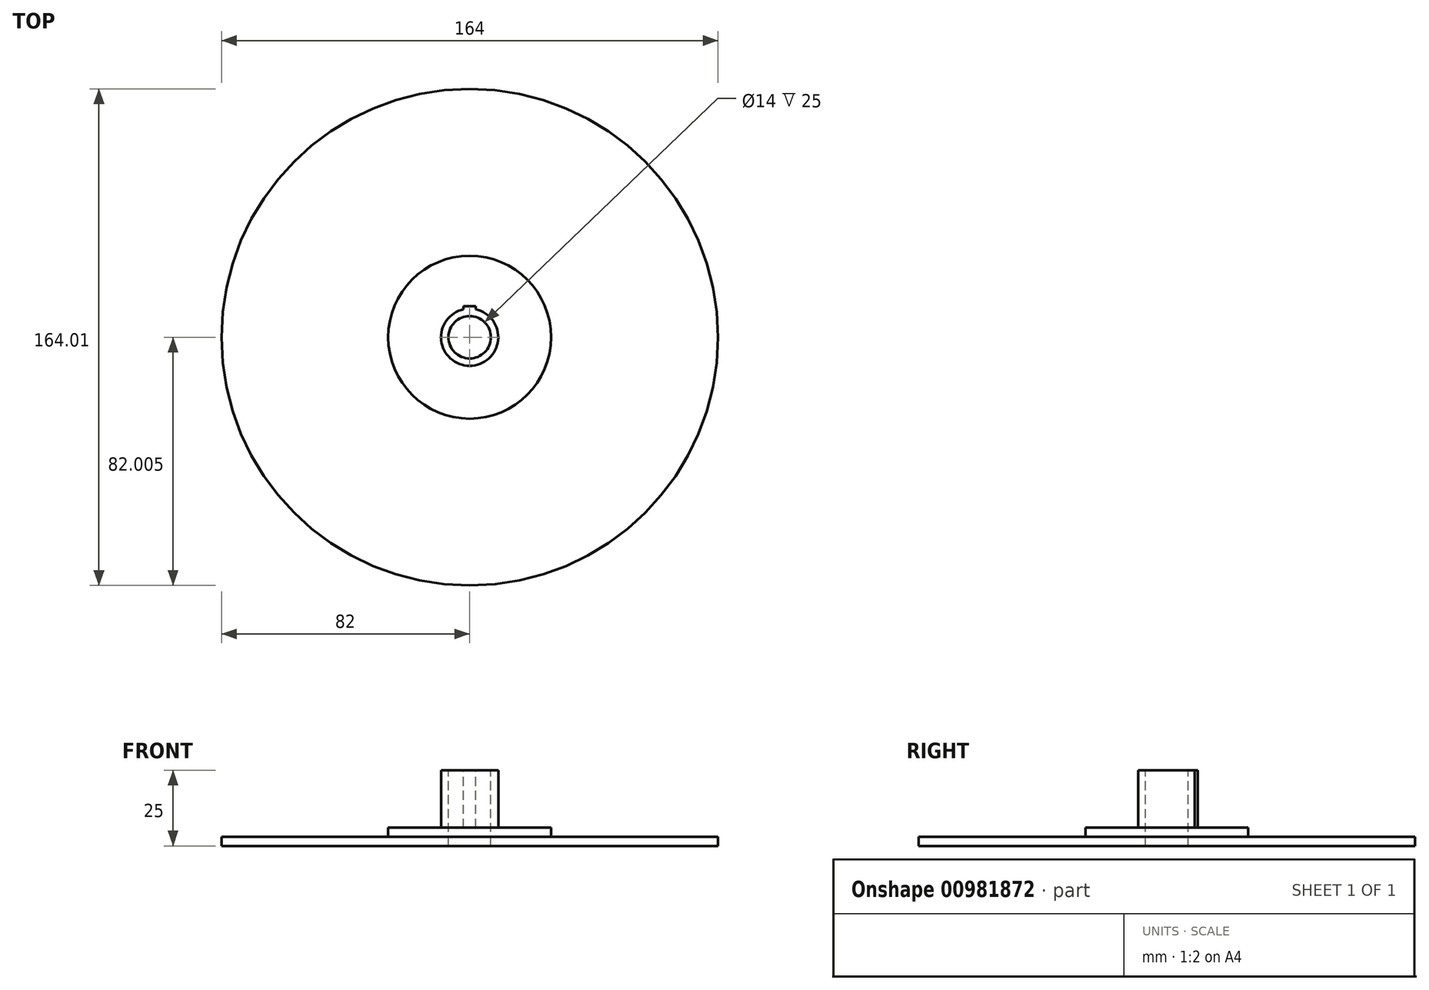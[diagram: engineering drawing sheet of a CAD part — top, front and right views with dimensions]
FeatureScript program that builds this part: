
annotation { "Feature Type Name" : "Feature", "Feature Type Description" : "" }
export const myFeature = defineFeature(function(context is Context, id is Id, definition is map)
    precondition{}
    {
        {
            var Q0;
            Q0=qCreatedBy(makeId("Top.planeOp"),FACE);
            var sketch = newSketch(context, id + "F0", { "sketchPlane" : qUnion([Q0])});
            skCircle(sketch, "E0", {"center": v(0, 0) * mm, "radius": 82 * mm});
            skSolve(sketch);
        }
        {
            var Q0;
            Q0=makeQuery(id+"F0.imprint","IMPRINT",FACE,{"disambiguationData":[TD([[makeQuery(id+"F0.imprint","IMPRINT",EDGE,{"derivedFrom":sQuery(id+"F0.wireOp",EDGE,"E0")}),1.0]])]});
            extrude(context, id + "F1", {"entities" : qUnion([Q0]), "oppositeDirection" : true, "depth" : 3 * mm, "offsetDistance" : 25 * mm});
        }
        {
            var Q0;
            Q0=makeQuery(id+"F1.opExtrude","CAP_FACE",FACE,{"disambiguationData":[OSD([sQuery(id+"F0.wireOp",EDGE,"E0")])],"isStart":true});
            var sketch = newSketch(context, id + "F2", { "sketchPlane" : qUnion([Q0])});
            skCircle(sketch, "E1", {"center": v(0, 0) * mm, "radius": 26.9 * mm});
            skSolve(sketch);
        }
        {
            var Q0;
            Q0=makeQuery(id+"F2.imprint","IMPRINT",FACE,{"disambiguationData":[TD([[makeQuery(id+"F2.imprint","IMPRINT",EDGE,{"derivedFrom":sQuery(id+"F2.wireOp",EDGE,"E1")}),1.0]])]});
            extrude(context, id + "F3", {"entities" : qUnion([Q0]), "operationType" : NewBodyOperationType.ADD, "depth" : 3 * mm, "offsetDistance" : 25 * mm});
        }
        {
            var Q0;
            Q0=makeQuery(id+"F3.opExtrude","CAP_FACE",FACE,{"disambiguationData":[OSD([sQuery(id+"F2.wireOp",EDGE,"E1")])],"isStart":false});
            var sketch = newSketch(context, id + "F4", { "sketchPlane" : qUnion([Q0])});
            skCircle(sketch, "E2", {"center": v(0, 0) * mm, "radius": 9.45 * mm});
            skSolve(sketch);
        }
        {
            var Q0;
            Q0=makeQuery(id+"F4.imprint","IMPRINT",FACE,{"disambiguationData":[TD([[makeQuery(id+"F4.imprint","IMPRINT",EDGE,{"derivedFrom":sQuery(id+"F4.wireOp",EDGE,"E2")}),1.0]])]});
            extrude(context, id + "F5", {"entities" : qUnion([Q0]), "operationType" : NewBodyOperationType.ADD, "depth" : 19 * mm, "offsetDistance" : 25 * mm});
        }
        {
            var Q0;
            Q0=makeQuery(id+"F5.opExtrude","CAP_FACE",FACE,{"disambiguationData":[OSD([sQuery(id+"F4.wireOp",EDGE,"E2")])],"isStart":false});
            var sketch = newSketch(context, id + "F6", { "sketchPlane" : qUnion([Q0])});
            skLineSegment(sketch, "E3.bottom", {"start": v(2, -5.73) * mm, "end": v(-2, -5.73) * mm});
            skLineSegment(sketch, "E3.top", {"start": v(2, 5.73) * mm, "end": v(-2, 5.73) * mm});
            skLineSegment(sketch, "E3.left", {"start": v(2, -5.73) * mm, "end": v(2, 5.73) * mm});
            skLineSegment(sketch, "E3.right", {"start": v(-2, -5.73) * mm, "end": v(-2, 5.73) * mm});
            skPoint(sketch, "E3.middle", {"position": v(0, 0) * mm});
            skSolve(sketch);
        }
        {
            var Q0;
            Q0=makeQuery(id+"F6.imprint","IMPRINT",FACE,{"disambiguationData":[TD([[makeQuery(id+"F6.imprint","IMPRINT",EDGE,{"derivedFrom":sQuery(id+"F6.wireOp",EDGE,"E3.bottom")}),-1.0]])]});
            extrude(context, id + "F7", {"entities" : qUnion([Q0]), "operationType" : NewBodyOperationType.ADD, "oppositeDirection" : true, "depth" : 19 * mm, "offsetDistance" : 25 * mm});
        }
        {
            var Q0;
            Q0=makeQuery(id+"F1.opExtrude","SWEPT_BODY",BODY,{"disambiguationData":[OSD([sQuery(id+"F0.wireOp",EDGE,"E0")])]});
            transform(context, id + "F8", {"entities" : qUnion([Q0]), "transformType" : TransformType.TRANSLATION_3D, "dx" : 0 * mm, "dy" : -5.72 * mm, "dz" : 0 * mm, "makeCopy" : false});
        }
        {
            var Q0;
            Q0=makeQuery(id+"F6.imprint","IMPRINT",FACE,{"disambiguationData":[TD([[makeQuery(id+"F6.imprint","IMPRINT",EDGE,{"derivedFrom":sQuery(id+"F6.wireOp",EDGE,"E3.bottom")}),-1.0]])]});
            extrude(context, id + "F9", {"entities" : qUnion([Q0]), "operationType" : NewBodyOperationType.ADD, "oppositeDirection" : true, "depth" : 20 * mm, "offsetDistance" : 25 * mm});
        }
        {
            var Q0;
            Q0=makeQuery(id+"F9.opExtrude","SWEPT_FACE",FACE,{"disambiguationData":[OSD([sQuery(id+"F6.wireOp",EDGE,"E3.top")])]});
            extrude(context, id + "F10", {"entities" : qUnion([Q0]), "operationType" : NewBodyOperationType.REMOVE, "oppositeDirection" : true, "depth" : 1.2 * mm, "offsetDistance" : 25 * mm});
        }
        {
            var Q0;
            Q0=makeQuery(id+"F9.boolean.opBoolean","MERGE",FACE,{"derivedFrom":[makeQuery(id+"F5.opExtrude","CAP_FACE",FACE,{"disambiguationData":[OSD([sQuery(id+"F4.wireOp",EDGE,"E2")])],"isStart":false}),makeQuery(id+"F9.opExtrude","CAP_FACE",FACE,{"disambiguationData":[OSD([sQuery(id+"F6.wireOp",EDGE,"E3.bottom"),sQuery(id+"F6.wireOp",EDGE,"E3.top"),sQuery(id+"F6.wireOp",EDGE,"E3.left"),sQuery(id+"F6.wireOp",EDGE,"E3.right")])],"isStart":true})]});
            var sketch = newSketch(context, id + "F11", { "sketchPlane" : qUnion([Q0])});
            skCircle(sketch, "E4", {"center": v(0, -5.72) * mm, "radius": 7 * mm});
            skSolve(sketch);
        }
        {
            var Q0;
            Q0=makeQuery(id+"F11.imprint","IMPRINT",FACE,{"disambiguationData":[TD([[makeQuery(id+"F11.imprint","IMPRINT",EDGE,{"derivedFrom":sQuery(id+"F11.wireOp",EDGE,"E4")}),1.0]])]});
            extrude(context, id + "F12", {"entities" : qUnion([Q0]), "operationType" : NewBodyOperationType.REMOVE, "oppositeDirection" : true, "depth" : 25 * mm, "offsetDistance" : 25 * mm});
        }
    });
